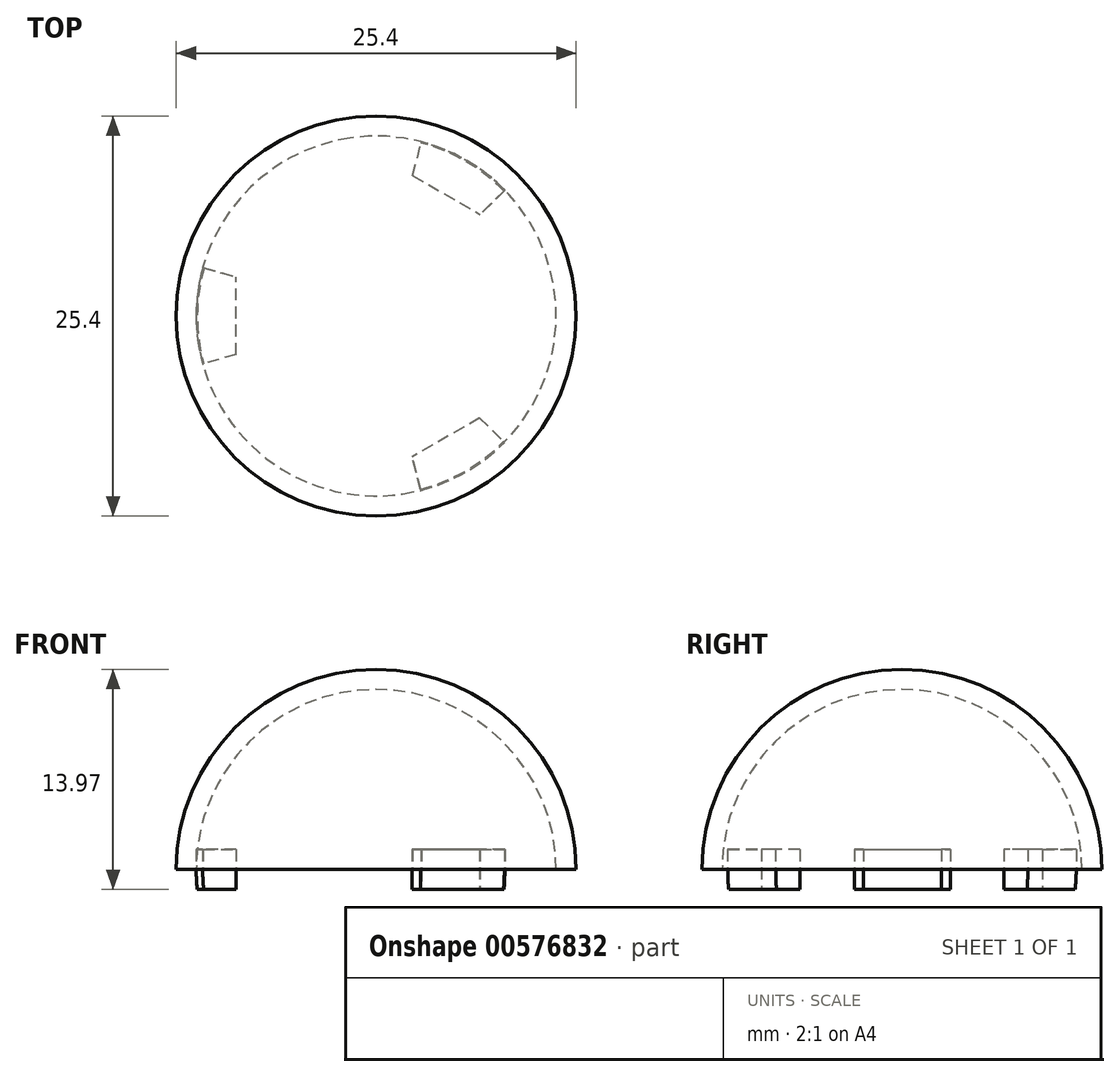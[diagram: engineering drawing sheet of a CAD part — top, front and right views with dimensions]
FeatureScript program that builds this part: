
annotation { "Feature Type Name" : "Feature", "Feature Type Description" : "" }
export const myFeature = defineFeature(function(context is Context, id is Id, definition is map)
    precondition{}
    {
        {
            var Q0;
            Q0=qCreatedBy(makeId("Top.planeOp"),FACE);
            var sketch = newSketch(context, id + "F0", { "sketchPlane" : qUnion([Q0])});
            skCircle(sketch, "E0", {"center": v(0, 0) * mm, "radius": 12.7 * mm});
            skLineSegment(sketch, "E1", {"start": v(0, 12.7) * mm, "end": v(0, -12.7) * mm});
            skSolve(sketch);
        }
        {
            var Q0;
            {var subQ0=sQuery(id+"F0.wireOp",EDGE,"E1");Q0=makeQuery(id+"F0.imprint","IMPRINT",FACE,{"disambiguationData":[TD([[makeQuery(id+"F0.imprint","IMPRINT",EDGE,{"derivedFrom":subQ0}),1.0]])]});}
            var Q1;
            Q1=sQuery(id+"F0.wireOp",EDGE,"E1");
            revolve(context, id + "F1", {"entities" : qUnion([Q0]), "axis" : qUnion([Q1]), "revolveType" : RevolveType.ONE_DIRECTION, "angle" : 180 * degree});
        }
        {
            var Q0;
            Q0=makeQuery(id+"F1.opRevolve","CAP_FACE",FACE,{"disambiguationData":[OSD([sQuery(id+"F0.wireOp",EDGE,"E0"),sQuery(id+"F0.wireOp",EDGE,"E1")])],"isStart":true});
            var sketch = newSketch(context, id + "F2", { "sketchPlane" : qUnion([Q0])});
            skCircle(sketch, "E2", {"center": v(0, 0) * mm, "radius": 11.43 * mm});
            skLineSegment(sketch, "E3", {"start": v(1.67, 11.3) * mm, "end": v(-1.67, -11.3) * mm});
            skSolve(sketch);
        }
        {
            var Q0;
            {var subQ0=sQuery(id+"F2.wireOp",EDGE,"E3");Q0=makeQuery(id+"F2.imprint","IMPRINT",FACE,{"disambiguationData":[TD([[makeQuery(id+"F2.imprint","IMPRINT",EDGE,{"derivedFrom":subQ0}),-1.0]])]});}
            var Q1;
            Q1=sQuery(id+"F2.wireOp",EDGE,"E3");
            revolve(context, id + "F3", {"operationType" : NewBodyOperationType.REMOVE, "entities" : qUnion([Q0]), "axis" : qUnion([Q1]), "revolveType" : RevolveType.ONE_DIRECTION, "angle" : 197.78 * degree});
        }
        {
            var Q0;
            Q0=makeQuery(id+"F1.opRevolve","CAP_FACE",FACE,{"disambiguationData":[OSD([sQuery(id+"F0.wireOp",EDGE,"E0"),sQuery(id+"F0.wireOp",EDGE,"E1")])],"isStart":true});
            var sketch = newSketch(context, id + "F4", { "sketchPlane" : qUnion([Q0])});
            skLineSegment(sketch, "E4.right", {"start": v(-11.43, 3.15) * mm, "end": v(-11.43, -3.2) * mm});
            skPoint(sketch, "E4.middle", {"position": v(-10.16, 0) * mm});
            skPoint(sketch, "E5.center", {"position": v(0, 0) * mm});
            skLineSegment(sketch, "E6", {"start": v(-8.89, 2.45) * mm, "end": v(-8.89, -2.49) * mm});
            skPoint(sketch, "E7", {"position": v(-11.43, 0) * mm});
            skLineSegment(sketch, "E8", {"start": v(-11.43, -3.2) * mm, "end": v(-8.89, -2.49) * mm});
            skLineSegment(sketch, "E9", {"start": v(-8.89, 2.45) * mm, "end": v(-11.43, 3.15) * mm});
            skLineSegment(sketch, "E10.1.0", {"start": v(2.32, -8.92) * mm, "end": v(2.99, -11.47) * mm});
            skLineSegment(sketch, "E10.1.1", {"start": v(2.32, -8.92) * mm, "end": v(6.6, -6.45) * mm});
            skLineSegment(sketch, "E10.1.2", {"start": v(2.99, -11.47) * mm, "end": v(8.49, -8.3) * mm});
            skLineSegment(sketch, "E10.1.3", {"start": v(8.49, -8.3) * mm, "end": v(6.6, -6.45) * mm});
            skLineSegment(sketch, "E10.2.0", {"start": v(6.57, 6.47) * mm, "end": v(8.44, 8.32) * mm});
            skLineSegment(sketch, "E10.2.1", {"start": v(6.57, 6.47) * mm, "end": v(2.29, 8.94) * mm});
            skLineSegment(sketch, "E10.2.2", {"start": v(8.44, 8.32) * mm, "end": v(2.94, 11.5) * mm});
            skLineSegment(sketch, "E10.2.3", {"start": v(2.94, 11.5) * mm, "end": v(2.29, 8.94) * mm});
            skSolve(sketch);
        }
        {
            var Q0;
            {var subQ1=sQuery(id+"F4.wireOp",EDGE,"E6");Q0=makeQuery(id+"F4.imprint","IMPRINT",FACE,{"disambiguationData":[TD([[makeQuery(id+"F4.imprint","IMPRINT",EDGE,{"derivedFrom":subQ1}),-1.0]])]});}
            var Q1;
            {var subQ5=sQuery(id+"F4.wireOp",EDGE,"E10.1.1");Q1=makeQuery(id+"F4.imprint","IMPRINT",FACE,{"disambiguationData":[TD([[makeQuery(id+"F4.imprint","IMPRINT",EDGE,{"derivedFrom":subQ5}),-1.0]])]});}
            var Q2;
            {var subQ1=sQuery(id+"F4.wireOp",EDGE,"E10.2.1");Q2=makeQuery(id+"F4.imprint","IMPRINT",FACE,{"disambiguationData":[TD([[makeQuery(id+"F4.imprint","IMPRINT",EDGE,{"derivedFrom":subQ1}),-1.0]])]});}
            extrude(context, id + "F5", {"entities" : qUnion([Q0, Q1, Q2]), "oppositeDirection" : true, "depth" : 1.27 * mm, "offsetDistance" : 25.4 * mm, "hasSecondDirection" : true, "secondDirectionOppositeDirection" : false, "secondDirectionDepth" : 1.27 * mm});
        }
        {
            var Q0;
            Q0=makeQuery(id+"F1.opRevolve","CAP_FACE",FACE,{"disambiguationData":[OSD([sQuery(id+"F0.wireOp",EDGE,"E0"),sQuery(id+"F0.wireOp",EDGE,"E1")])],"isStart":true});
            var sketch = newSketch(context, id + "F6", { "sketchPlane" : qUnion([Q0])});
            skCircle(sketch, "E11", {"center": v(0, 0) * mm, "radius": 11.43 * mm});
            skCircle(sketch, "E12", {"center": v(0, 0) * mm, "radius": 25.4 * mm});
            skLineSegment(sketch, "E13", {"start": v(-23.43, 9.81) * mm, "end": v(23.43, -9.81) * mm});
            skSolve(sketch);
        }
        {
            var Q0;
            {var subQ0=sQuery(id+"F6.wireOp",EDGE,"E13");var subQ1=sQuery(id+"F6.wireOp",EDGE,"E11");var subQ2=makeQuery(id+"F6.imprint","INTERSECT",VERTEX,{"disambiguationData":[OD(0.0)],"derivedFrom":[subQ1,subQ0]});Q0=makeQuery(id+"F6.imprint","IMPRINT",FACE,{"disambiguationData":[TD([[makeQuery(id+"F6.imprint","IMPRINT",EDGE,{"disambiguationData":[TD([[subQ2,1.0]])],"derivedFrom":subQ1}),-1.0]])]});}
            var Q1;
            {var subQ0=sQuery(id+"F6.wireOp",EDGE,"E13");var subQ1=sQuery(id+"F6.wireOp",EDGE,"E12");var subQ2=makeQuery(id+"F6.imprint","INTERSECT",VERTEX,{"disambiguationData":[OD(0.0)],"derivedFrom":[subQ1,subQ0]});Q1=makeQuery(id+"F6.imprint","IMPRINT",FACE,{"disambiguationData":[TD([[makeQuery(id+"F6.imprint","IMPRINT",EDGE,{"disambiguationData":[TD([[subQ2,1.0]])],"derivedFrom":subQ1}),1.0]])]});}
            var Q2;
            Q2=sQuery(id+"F6.wireOp",EDGE,"E13");
            revolve(context, id + "F7", {"operationType" : NewBodyOperationType.REMOVE, "entities" : qUnion([Q0, Q1]), "axis" : qUnion([Q2]), "revolveType" : RevolveType.ONE_DIRECTION, "angle" : 180 * degree});
        }
    });
